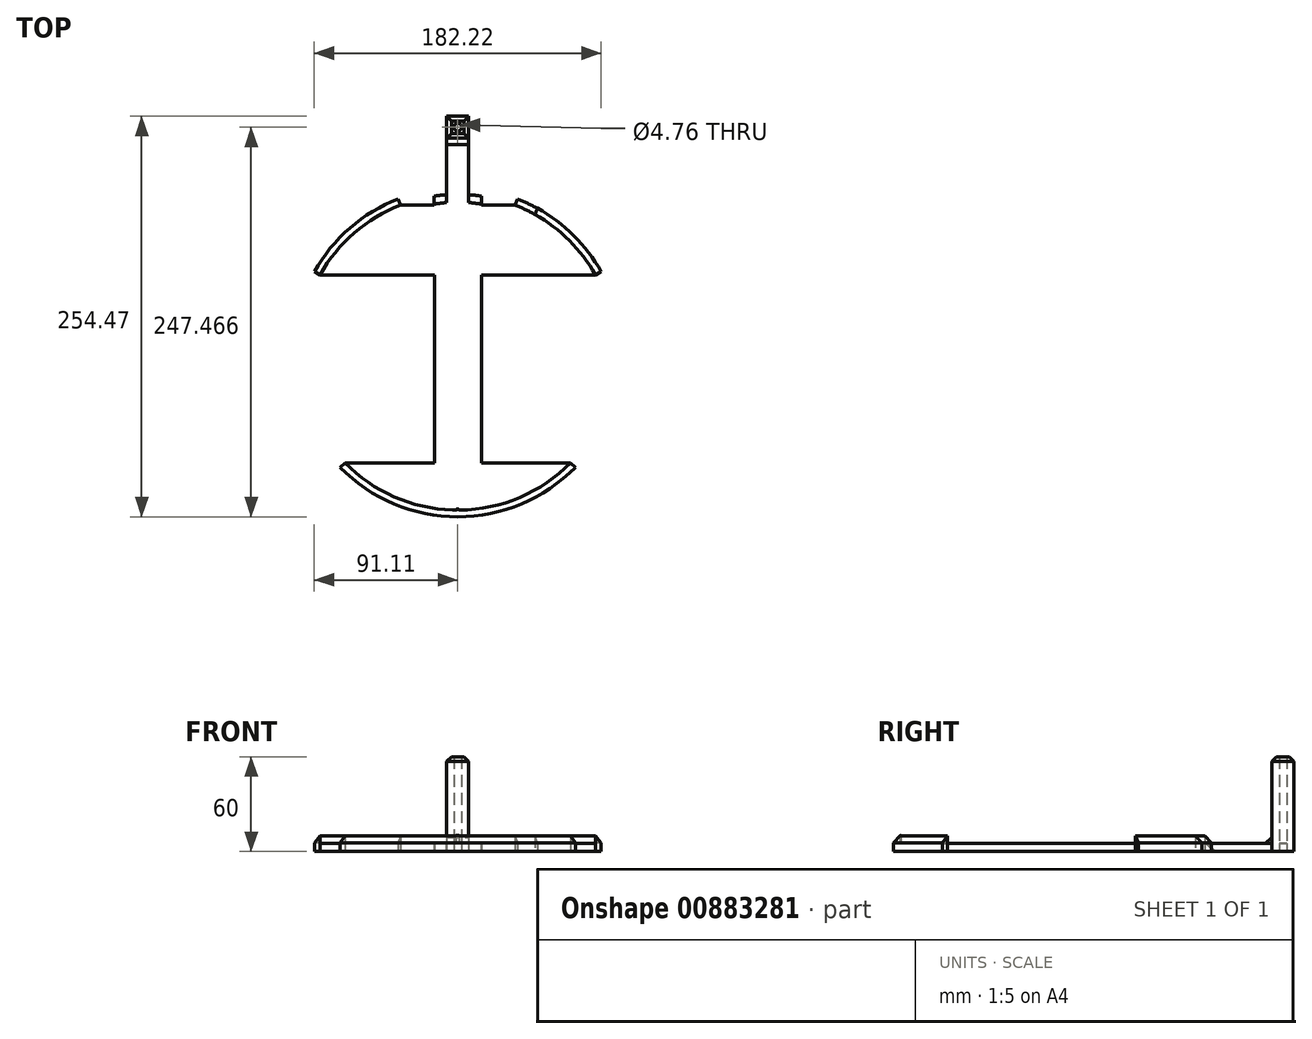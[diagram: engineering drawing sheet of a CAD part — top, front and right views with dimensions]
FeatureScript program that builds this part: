
annotation { "Feature Type Name" : "Feature", "Feature Type Description" : "" }
export const myFeature = defineFeature(function(context is Context, id is Id, definition is map)
    precondition{}
    {
        {
            var Q0;
            Q0=qCreatedBy(makeId("Top.planeOp"),FACE);
            var sketch = newSketch(context, id + "F0", { "sketchPlane" : qUnion([Q0])});
            skArc(sketch, "E0", {"start": v(87.44, 49.13) * mm, "mid": v(65.74, 75.75) * mm, "end": v(36.33, 93.49) * mm});
            skLineSegment(sketch, "E1", {"start": v(87.44, 49.13) * mm, "end": v(15.12, 49.13) * mm});
            skLineSegment(sketch, "E2", {"start": v(71.65, -70.19) * mm, "end": v(15.12, -70.19) * mm});
            skLineSegment(sketch, "E3", {"start": v(-14.97, 99.18) * mm, "end": v(-14.97, 93.49) * mm});
            skLineSegment(sketch, "E4", {"start": v(14.97, 99.18) * mm, "end": v(15, 93.49) * mm});
            skLineSegment(sketch, "E5", {"start": v(-36.33, 93.49) * mm, "end": v(-14.97, 93.49) * mm});
            skLineSegment(sketch, "E6.trimOffspring", {"start": v(15, 93.49) * mm, "end": v(36.33, 93.49) * mm});
            skArc(sketch, "E7", {"start": v(-74.65, -73.13) * mm, "mid": v(0, -104.5) * mm, "end": v(74.65, -73.13) * mm});
            skLineSegment(sketch, "E8", {"start": v(-87.44, 49.13) * mm, "end": v(-91.1, 51.19) * mm});
            skLineSegment(sketch, "E9", {"start": v(-36.33, 93.49) * mm, "end": v(-37.85, 97.4) * mm});
            skLineSegment(sketch, "E10", {"start": v(36.33, 93.49) * mm, "end": v(37.85, 97.4) * mm});
            skLineSegment(sketch, "E11", {"start": v(87.44, 49.13) * mm, "end": v(91.1, 51.19) * mm});
            skLineSegment(sketch, "E12", {"start": v(71.65, -70.19) * mm, "end": v(74.65, -73.13) * mm});
            skLineSegment(sketch, "E13", {"start": v(-71.65, -70.19) * mm, "end": v(-74.65, -73.13) * mm});
            skArc(sketch, "E14.trimOffspring", {"start": v(91.1, 51.19) * mm, "mid": v(68.5, 78.92) * mm, "end": v(37.85, 97.4) * mm});
            skArc(sketch, "E15.trimOffspring", {"start": v(-37.85, 97.4) * mm, "mid": v(-68.5, 78.92) * mm, "end": v(-91.1, 51.19) * mm});
            skLineSegment(sketch, "E16", {"start": v(-14.88, -70.19) * mm, "end": v(-14.88, 49.13) * mm});
            skLineSegment(sketch, "E17", {"start": v(15.12, -70.19) * mm, "end": v(15.12, 49.13) * mm});
            skLineSegment(sketch, "E18.trimOffspring", {"start": v(-14.88, 49.13) * mm, "end": v(-87.44, 49.13) * mm});
            skLineSegment(sketch, "E19.trimOffspring", {"start": v(-14.88, -70.19) * mm, "end": v(-71.65, -70.19) * mm});
            skArc(sketch, "E20.trimOffspring", {"start": v(-71.65, -70.19) * mm, "mid": v(-40.4, -91.8) * mm, "end": v(-3.37, -100.24) * mm});
            skArc(sketch, "E21.trimOffspring", {"start": v(-36.33, 93.49) * mm, "mid": v(-65.74, 75.75) * mm, "end": v(-87.44, 49.13) * mm});
            skArc(sketch, "E22.trimOffspring", {"start": v(14.97, 99.18) * mm, "mid": v(0, 100.3) * mm, "end": v(-14.97, 99.18) * mm});
            skArc(sketch, "E23.trimOffspring", {"start": v(1.32, -100.3) * mm, "mid": v(39.47, -92.2) * mm, "end": v(71.65, -70.19) * mm});
            skLineSegment(sketch, "E24", {"start": v(0, 0) * mm, "end": v(0, 100.5) * mm});
            skArc(sketch, "E25", {"start": v(-3.37, -100.24) * mm, "mid": v(-1.02, -100.3) * mm, "end": v(1.32, -100.3) * mm});
            skLineSegment(sketch, "E26", {"start": v(-1.09, -100.3) * mm, "end": v(-1.09, -100.28) * mm});
            skLineSegment(sketch, "E27", {"start": v(0.91, -100.3) * mm, "end": v(0.91, -100.28) * mm});
            skLineSegment(sketch, "E28", {"start": v(-1.02, -100.3) * mm, "end": v(-1.02, -100.1) * mm});
            skArc(sketch, "E29", {"start": v(0.91, -100.3) * mm, "mid": v(-0.09, -99.49) * mm, "end": v(-1.09, -100.3) * mm});
            skLineSegment(sketch, "E30", {"start": v(36.33, 93.49) * mm, "end": v(37.1, 95.45) * mm});
            skLineSegment(sketch, "E31", {"start": v(37.85, 97.4) * mm, "end": v(55.96, 144) * mm});
            skLineSegment(sketch, "E32", {"start": v(37.85, 97.4) * mm, "end": v(44.38, 94.87) * mm});
            skCircle(sketch, "E33", {"center": v(46.91, 101.4) * mm, "radius": 2.38 * mm});
            skLineSegment(sketch, "E34", {"start": v(55.96, 144) * mm, "end": v(58.5, 150.53) * mm});
            skArc(sketch, "E35", {"start": v(70.75, 144.95) * mm, "mid": v(64.7, 147.92) * mm, "end": v(58.5, 150.53) * mm});
            skLineSegment(sketch, "E36.MirrorCS", {"start": v(50.56, 91.45) * mm, "end": v(70.75, 144.95) * mm});
            skPoint(sketch, "E37.orphan", {"position": v(49.4, 88.4) * mm});
            skLineSegment(sketch, "E38", {"start": v(70.75, 144.95) * mm, "end": v(49.06, 87.48) * mm});
            skCircle(sketch, "E39", {"center": v(52.82, 118.76) * mm, "radius": 2.38 * mm});
            skCircle(sketch, "E40", {"center": v(55.9, 127.43) * mm, "radius": 2.38 * mm});
            skCircle(sketch, "E41", {"center": v(58.95, 135.17) * mm, "radius": 2.38 * mm});
            skCircle(sketch, "E42", {"center": v(62.98, 142.92) * mm, "radius": 2.38 * mm});
            skCircle(sketch, "E43", {"center": v(50.03, 110.47) * mm, "radius": 2.38 * mm});
            skLineSegment(sketch, "E44", {"start": v(0, 135.97) * mm, "end": v(7, 135.97) * mm});
            skLineSegment(sketch, "E45", {"start": v(0, 135.97) * mm, "end": v(0, 142.97) * mm});
            skCircle(sketch, "E46", {"center": v(0, 142.97) * mm, "radius": 2.38 * mm});
            skLineSegment(sketch, "E47", {"start": v(7, 135.97) * mm, "end": v(7, 149.97) * mm});
            skLineSegment(sketch, "E48", {"start": v(7, 149.97) * mm, "end": v(-7, 149.97) * mm});
            skLineSegment(sketch, "E49", {"start": v(-7, 149.97) * mm, "end": v(-7, 135.97) * mm});
            skLineSegment(sketch, "E50", {"start": v(7, 135.97) * mm, "end": v(7, 97.25) * mm});
            skLineSegment(sketch, "E51", {"start": v(-7, 135.97) * mm, "end": v(-7, 93.49) * mm});
            skLineSegment(sketch, "E52", {"start": v(-14.97, 93.49) * mm, "end": v(15, 93.49) * mm});
            skLineSegment(sketch, "E53", {"start": v(7, 97.25) * mm, "end": v(7, 93.49) * mm});
            skLineSegment(sketch, "E54", {"start": v(-7, 135.97) * mm, "end": v(7, 135.97) * mm});
            skSolve(sketch);
        }
        {
            var Q0;
            Q0=makeQuery(id+"F0.imprint","IMPRINT",FACE,{"disambiguationData":[TD([[makeQuery(id+"F0.imprint","IMPRINT",EDGE,{"derivedFrom":sQuery(id+"F0.wireOp",EDGE,"E0")}),1.0]])]});
            extrude(context, id + "F1", {"entities" : qUnion([Q0]), "depth" : 5 * mm, "offsetDistance" : 25 * mm});
        }
        {
            var Q0;
            Q0=makeQuery(id+"F0.imprint","IMPRINT",FACE,{"disambiguationData":[TD([[makeQuery(id+"F0.imprint","IMPRINT",EDGE,{"derivedFrom":sQuery(id+"F0.wireOp",EDGE,"E8")}),-1.0]])]});
            var Q1;
            Q1=makeQuery(id+"F0.imprint","IMPRINT",FACE,{"disambiguationData":[TD([[makeQuery(id+"F0.imprint","IMPRINT",EDGE,{"derivedFrom":sQuery(id+"F0.wireOp",EDGE,"E7")}),1.0]])]});
            extrude(context, id + "F2", {"entities" : qUnion([Q0, Q1]), "operationType" : NewBodyOperationType.ADD, "depth" : 10 * mm, "offsetDistance" : 25 * mm});
        }
        {
            var Q0;
            {var subQ3=sQuery(id+"F0.wireOp",EDGE,"E28");Q0=makeQuery(id+"F0.imprint","IMPRINT",FACE,{"disambiguationData":[TD([[makeQuery(id+"F0.imprint","IMPRINT",EDGE,{"derivedFrom":subQ3}),1.0]])]});}
            var Q1;
            {var subQ3=sQuery(id+"F0.wireOp",EDGE,"E28");Q1=makeQuery(id+"F0.imprint","IMPRINT",FACE,{"disambiguationData":[TD([[makeQuery(id+"F0.imprint","IMPRINT",EDGE,{"derivedFrom":subQ3}),-1.0]])]});}
            extrude(context, id + "F3", {"entities" : qUnion([Q0, Q1]), "operationType" : NewBodyOperationType.ADD, "depth" : 10 * mm, "offsetDistance" : 25 * mm});
        }
        {
            var Q0;
            Q0=makeQuery(id+"F2.opExtrude","CAP_EDGE",EDGE,{"disambiguationData":[OSD([sQuery(id+"F0.wireOp",EDGE,"E7")])],"isStart":false});
            chamfer(context, id + "F4", {"entities" : qUnion([Q0]), "width" : 4.5 * mm, "tangentPropagation" : true});
        }
        {
            var Q0;
            Q0=makeQuery(id+"F2.opExtrude","CAP_EDGE",EDGE,{"disambiguationData":[OSD([sQuery(id+"F0.wireOp",EDGE,"E15.trimOffspring")])],"isStart":false});
            chamfer(context, id + "F5", {"entities" : qUnion([Q0]), "width" : 4.5 * mm, "tangentPropagation" : true});
        }
        {
            var Q0;
            {var subQ1=sQuery(id+"F0.wireOp",EDGE,"E10");Q0=makeQuery(id+"F0.imprint","IMPRINT",FACE,{"disambiguationData":[TD([[makeQuery(id+"F0.imprint","IMPRINT",EDGE,{"derivedFrom":subQ1}),-1.0]])]});}
            extrude(context, id + "F6", {"entities" : qUnion([Q0]), "depth" : 10 * mm, "offsetDistance" : 25 * mm});
        }
        {
            var Q0;
            {var subQ0=sQuery(id+"F0.wireOp",EDGE,"E11");Q0=makeQuery(id+"F0.imprint","IMPRINT",FACE,{"disambiguationData":[TD([[makeQuery(id+"F0.imprint","IMPRINT",EDGE,{"derivedFrom":subQ0}),1.0]])]});}
            extrude(context, id + "F7", {"entities" : qUnion([Q0]), "depth" : 10 * mm, "offsetDistance" : 25 * mm});
        }
        {
            var Q0;
            Q0=makeQuery(id+"F7.opExtrude","CAP_EDGE",EDGE,{"disambiguationData":[OSD([sQuery(id+"F0.wireOp",EDGE,"E14.trimOffspring")])],"isStart":false});
            chamfer(context, id + "F8", {"entities" : qUnion([Q0]), "width" : 4.5 * mm, "tangentPropagation" : true});
        }
        {
            var Q0;
            {var subQ0=sQuery(id+"F0.wireOp",EDGE,"E24");var subQ1=sQuery(id+"F0.wireOp",EDGE,"E22.trimOffspring");var subQ2=makeQuery(id+"F0.imprint","INTERSECT",VERTEX,{"derivedFrom":[subQ1,subQ0]});Q0=makeQuery(id+"F0.imprint","IMPRINT",FACE,{"disambiguationData":[TD([[makeQuery(id+"F0.imprint","IMPRINT",EDGE,{"disambiguationData":[TD([[subQ2,-1.0]])],"derivedFrom":subQ1}),1.0]])]});}
            var Q1;
            {var subQ0=sQuery(id+"F0.wireOp",EDGE,"E53");Q1=makeQuery(id+"F0.imprint","IMPRINT",FACE,{"disambiguationData":[TD([[makeQuery(id+"F0.imprint","IMPRINT",EDGE,{"derivedFrom":subQ0}),-1.0]])]});}
            var Q2;
            {var subQ1=sQuery(id+"F0.wireOp",EDGE,"E50");var subQ3=sQuery(id+"F0.wireOp",EDGE,"E22.trimOffspring");var subQ4=makeQuery(id+"F0.imprint","INTERSECT",VERTEX,{"derivedFrom":[subQ3,subQ1]});Q2=makeQuery(id+"F0.imprint","IMPRINT",FACE,{"disambiguationData":[TD([[makeQuery(id+"F0.imprint","IMPRINT",EDGE,{"disambiguationData":[TD([[subQ4,-1.0]])],"derivedFrom":subQ3}),-1.0]])]});}
            extrude(context, id + "F9", {"entities" : qUnion([Q0, Q1, Q2]), "operationType" : NewBodyOperationType.ADD, "depth" : 5 * mm, "offsetDistance" : 25 * mm});
        }
        {
            var Q0;
            {var subQ0=sQuery(id+"F0.wireOp",EDGE,"E3");Q0=makeQuery(id+"F0.imprint","IMPRINT",FACE,{"disambiguationData":[TD([[makeQuery(id+"F0.imprint","IMPRINT",EDGE,{"derivedFrom":subQ0}),1.0]])]});}
            var Q1;
            {var subQ4=sQuery(id+"F0.wireOp",EDGE,"E4");Q1=makeQuery(id+"F0.imprint","IMPRINT",FACE,{"disambiguationData":[TD([[makeQuery(id+"F0.imprint","IMPRINT",EDGE,{"derivedFrom":subQ4}),-1.0]])]});}
            extrude(context, id + "F10", {"entities" : qUnion([Q0, Q1]), "operationType" : NewBodyOperationType.ADD, "depth" : 5 * mm, "offsetDistance" : 25 * mm});
        }
        {
            var Q0;
            Q0=makeQuery(id+"F0.imprint","IMPRINT",FACE,{"disambiguationData":[TD([[makeQuery(id+"F0.imprint","IMPRINT",EDGE,{"derivedFrom":sQuery(id+"F0.wireOp",EDGE,"E46")}),1.0]])]});
            extrude(context, id + "F11", {"entities" : qUnion([Q0]), "depth" : 5 * mm, "offsetDistance" : 25 * mm});
        }
        {
            var Q0;
            Q0=makeQuery(id+"F0.imprint","IMPRINT",FACE,{"disambiguationData":[TD([[makeQuery(id+"F0.imprint","IMPRINT",EDGE,{"derivedFrom":sQuery(id+"F0.wireOp",EDGE,"E46")}),-1.0]])]});
            extrude(context, id + "F12", {"entities" : qUnion([Q0]), "depth" : 60 * mm, "offsetDistance" : 25 * mm});
        }
        {
            var Q0;
            Q0=makeQuery(id+"F6.opExtrude","CAP_EDGE",EDGE,{"disambiguationData":[OSD([sQuery(id+"F0.wireOp",EDGE,"E14.trimOffspring")])],"isStart":false});
            chamfer(context, id + "F13", {"entities" : qUnion([Q0]), "width" : 4.5 * mm, "tangentPropagation" : true});
        }
        {
            var Q0;
            {var subQ0=sQuery(id+"F0.wireOp",EDGE,"E22.trimOffspring");Q0=makeQuery(id+"F10.opExtrude","CAP_EDGE",EDGE,{"disambiguationData":[OSD([subQ0]),TDD([makeQuery(id+"F0.imprint","IMPRINT",EDGE,{"disambiguationData":[TD([[makeQuery(id+"F0.imprint","INTERSECT",VERTEX,{"derivedFrom":[sQuery(id+"F0.wireOp",EDGE,"E3"),subQ0]}),1.0]])],"derivedFrom":subQ0})])],"isStart":false});}
            chamfer(context, id + "F14", {"entities" : qUnion([Q0]), "width" : 5 * mm, "tangentPropagation" : true});
        }
        {
            var Q0;
            {var subQ0=sQuery(id+"F0.wireOp",EDGE,"E22.trimOffspring");Q0=makeQuery(id+"F10.opExtrude","CAP_EDGE",EDGE,{"disambiguationData":[OSD([subQ0]),TDD([makeQuery(id+"F0.imprint","IMPRINT",EDGE,{"disambiguationData":[TD([[makeQuery(id+"F0.imprint","INTERSECT",VERTEX,{"derivedFrom":[sQuery(id+"F0.wireOp",EDGE,"E4"),subQ0]}),-1.0]])],"derivedFrom":subQ0})])],"isStart":false});}
            chamfer(context, id + "F15", {"entities" : qUnion([Q0]), "width" : 5 * mm, "tangentPropagation" : true});
        }
        {
            var Q0;
            Q0=makeQuery(id+"F12.opExtrude","CAP_EDGE",EDGE,{"disambiguationData":[OSD([sQuery(id+"F0.wireOp",EDGE,"E54")])],"isStart":false});
            var Q1;
            Q1=makeQuery(id+"F12.opExtrude","CAP_EDGE",EDGE,{"disambiguationData":[OSD([sQuery(id+"F0.wireOp",EDGE,"E47")])],"isStart":false});
            var Q2;
            Q2=makeQuery(id+"F12.opExtrude","CAP_EDGE",EDGE,{"disambiguationData":[OSD([sQuery(id+"F0.wireOp",EDGE,"E48")])],"isStart":false});
            var Q3;
            Q3=makeQuery(id+"F12.opExtrude","CAP_EDGE",EDGE,{"disambiguationData":[OSD([sQuery(id+"F0.wireOp",EDGE,"E49")])],"isStart":false});
            chamfer(context, id + "F16", {"entities" : qUnion([Q0, Q1, Q2, Q3]), "width" : 3 * mm, "tangentPropagation" : true});
        }
        {
            var Q0;
            Q0=makeQuery(id+"F12.opExtrude","SWEPT_FACE",FACE,{"disambiguationData":[OSD([sQuery(id+"F0.wireOp",EDGE,"E47")])]});
            var sketch = newSketch(context, id + "F17", { "sketchPlane" : qUnion([Q0])});
            skLineSegment(sketch, "E55", {"start": v(135.97, 0) * mm, "end": v(135.97, 5) * mm});
            skLineSegment(sketch, "E56", {"start": v(135.97, 5) * mm, "end": v(131.97, 5) * mm});
            skLineSegment(sketch, "E57", {"start": v(135.97, 5) * mm, "end": v(135.97, 9) * mm});
            skLineSegment(sketch, "E58", {"start": v(135.97, 9) * mm, "end": v(131.97, 5) * mm});
            skSolve(sketch);
        }
        {
            var Q0;
            Q0 = qSketchRegion(id + "F17", true);
            extrude(context, id + "F18", {"entities" : qUnion([Q0]), "oppositeDirection" : true, "depth" : 14 * mm, "offsetDistance" : 25 * mm});
        }
    });
